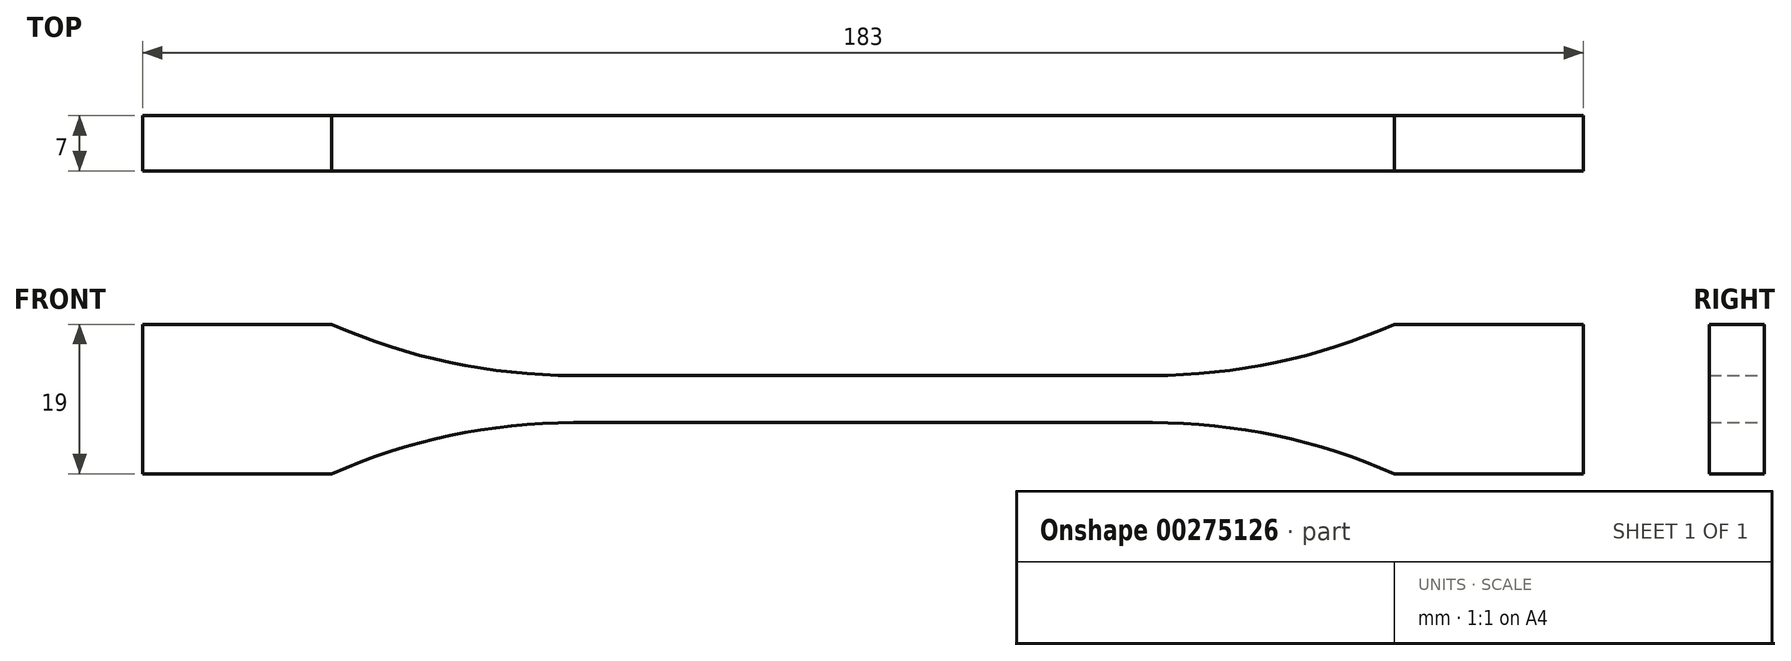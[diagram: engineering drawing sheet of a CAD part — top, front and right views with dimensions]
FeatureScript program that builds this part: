
annotation { "Feature Type Name" : "Feature", "Feature Type Description" : "" }
export const myFeature = defineFeature(function(context is Context, id is Id, definition is map)
    precondition{}
    {
        {
            var Q0;
            Q0=qCreatedBy(makeId("Front.planeOp"),FACE);
            var sketch = newSketch(context, id + "F0", { "sketchPlane" : qUnion([Q0])});
            skLineSegment(sketch, "E0", {"start": v(0, 3) * mm, "end": v(36.75, 3) * mm});
            skArc(sketch, "E1", {"start": v(36.75, 3) * mm, "mid": v(52.46, 4.64) * mm, "end": v(67.5, 9.5) * mm});
            skLineSegment(sketch, "E2", {"start": v(67.5, 9.5) * mm, "end": v(91.5, 9.5) * mm});
            skLineSegment(sketch, "E3", {"start": v(91.5, 9.5) * mm, "end": v(91.5, 0) * mm});
            skLineSegment(sketch, "E4.MirrorCS", {"start": v(0, -3) * mm, "end": v(36.75, -3) * mm});
            skLineSegment(sketch, "E5.MirrorCS", {"start": v(91.5, -9.5) * mm, "end": v(91.5, 0) * mm});
            skLineSegment(sketch, "E6.MirrorCS", {"start": v(67.5, -9.5) * mm, "end": v(91.5, -9.5) * mm});
            skArc(sketch, "E7.MirrorCS", {"start": v(36.75, -3) * mm, "mid": v(52.46, -4.64) * mm, "end": v(67.5, -9.5) * mm});
            skArc(sketch, "E8.MirrorCS", {"start": v(-36.75, -3) * mm, "mid": v(-52.46, -4.64) * mm, "end": v(-67.5, -9.5) * mm});
            skLineSegment(sketch, "E9.MirrorCS", {"start": v(-67.5, -9.5) * mm, "end": v(-91.5, -9.5) * mm});
            skArc(sketch, "E10.MirrorCS", {"start": v(-36.75, 3) * mm, "mid": v(-52.46, 4.64) * mm, "end": v(-67.5, 9.5) * mm});
            skLineSegment(sketch, "E11.MirrorCS", {"start": v(-67.5, 9.5) * mm, "end": v(-91.5, 9.5) * mm});
            skLineSegment(sketch, "E12.MirrorCS", {"start": v(-91.5, -9.5) * mm, "end": v(-91.5, 0) * mm});
            skLineSegment(sketch, "E13.MirrorCS", {"start": v(0, -3) * mm, "end": v(-36.75, -3) * mm});
            skLineSegment(sketch, "E14.MirrorCS", {"start": v(-91.5, 9.5) * mm, "end": v(-91.5, 0) * mm});
            skLineSegment(sketch, "E15.MirrorCS", {"start": v(0, 3) * mm, "end": v(-36.75, 3) * mm});
            skSolve(sketch);
        }
        {
            var Q0;
            Q0 = qSketchRegion(id + "F0", true);
            extrude(context, id + "F1", {"entities" : qUnion([Q0]), "endBound" : BoundingType.SYMMETRIC, "depth" : 7 * mm});
        }
    });
